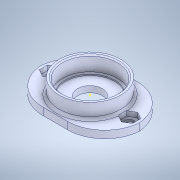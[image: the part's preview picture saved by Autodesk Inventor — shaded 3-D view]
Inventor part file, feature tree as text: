
AUTODESK INVENTOR PART (.ipt)
format: ipt  version: 2021 (Build 250183000, 183)  size: 215,040 bytes
history: mixed  units: in
note: dims shown in document units (in); Inventor stores cm internally (conversion verified against a paired STEP export)
features: sketch x7, extrude x5, delete_face x1, chamfer x1, fillet x1, other x1, imported_body x1
ambient origin geometry x8: Origin, YZ Plane, XZ Plane, XY Plane, X Axis, Y Axis, Z Axis, Center Point
bodies: Solid1 (imported_parasolid)
feature tree (17):
  extrude  "Extrusion1"  Depth=0.3937in TaperAngle=0.0deg
  extrude  "Extrusion2"  TaperAngle=0.0deg  [1 undecoded]
  sketch  "Sketch5"  dims[d8=0.9843in d9=0.3937in d10=0.0in]
  delete_face  "Delete Face1"
  extrude  "Extrusion4"  Depth=0.3937in TaperAngle=0.0deg
  extrude  "Extrusion5"  Depth=0.3937in TaperAngle=0.0deg
  chamfer  "Chamfer1"  Distance=0.0787in Angle=45.0deg
  sketch  "Sketch8"
  fillet  "Fillet1"  Radius=0.0394in
  extrude  "Extrusion8"  Depth=0.3937in TaperAngle=0.0deg
  sketch  "Sketch1"  dims[d0=0.7874in d1=0.3937in d2=0.0in]
  sketch  "Sketch2"  dims[d3=0.3937in d4=0.0in d5=0.0in]
  sketch  "Sketch6"  dims[d11=0.878in d12=0.3937in d13=0.0in d14=0.0197in d15=0.0787in d16=45.0deg d20=0.0394in]
  sketch  "Sketch7"  dims[d31=0.1378in d32=0.3937in d33=0.0in]
  sketch  "Sketch13"
  other  "Cut-Extrude3"
  imported_body  NMx_Import_Brep_tag  [imported B-rep: ~12 faces, bbox_mm=[32.0, 1.0, 0.0]]
note: 1 required parameter value undecoded (feature->parameter linkage not recoverable at this tier; creation-order binding heuristic only, values carry confidence <= 0.55)
